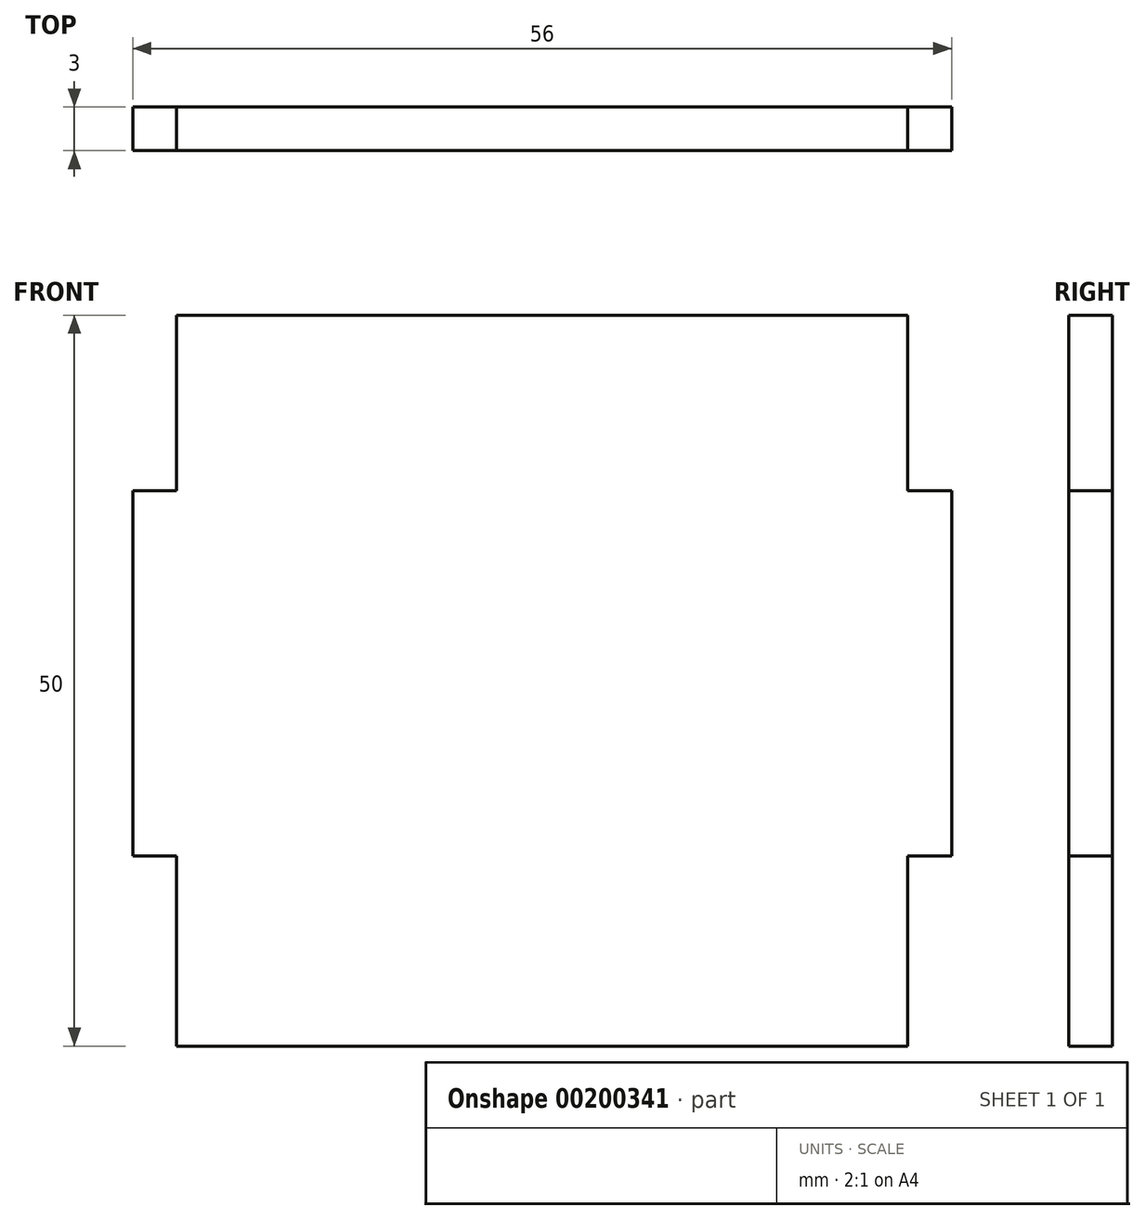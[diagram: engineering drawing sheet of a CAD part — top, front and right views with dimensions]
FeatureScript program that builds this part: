
annotation { "Feature Type Name" : "Feature", "Feature Type Description" : "" }
export const myFeature = defineFeature(function(context is Context, id is Id, definition is map)
    precondition{}
    {
        {
            var Q0;
            Q0=qCreatedBy(makeId("Front.planeOp"),FACE);
            var sketch = newSketch(context, id + "F0", { "sketchPlane" : qUnion([Q0])});
            skLineSegment(sketch, "E0.bottom", {"start": v(-60.5, 25.67) * mm, "end": v(-10.5, 25.67) * mm});
            skLineSegment(sketch, "E0.top", {"start": v(-60.5, -24.33) * mm, "end": v(-10.5, -24.33) * mm});
            skLineSegment(sketch, "E0.left", {"start": v(-60.5, 25.67) * mm, "end": v(-60.5, -24.33) * mm});
            skLineSegment(sketch, "E0.right", {"start": v(-10.5, 25.67) * mm, "end": v(-10.5, -24.33) * mm});
            skSolve(sketch);
        }
        {
            var Q0;
            Q0 = qSketchRegion(id + "F0", true);
            extrude(context, id + "F1", {"entities" : qUnion([Q0]), "depth" : 3 * mm});
        }
        {
            var Q0;
            Q0=makeQuery(id+"F1.opExtrude","SWEPT_FACE",FACE,{"disambiguationData":[OSD([sQuery(id+"F0.wireOp",EDGE,"E0.right")])]});
            var sketch = newSketch(context, id + "F2", { "sketchPlane" : qUnion([Q0])});
            skLineSegment(sketch, "E1.bottom", {"start": v(-3, 13.67) * mm, "end": v(0, 13.67) * mm});
            skLineSegment(sketch, "E1.top", {"start": v(-3, -11.33) * mm, "end": v(0, -11.33) * mm});
            skLineSegment(sketch, "E1.left", {"start": v(-3, 13.67) * mm, "end": v(-3, -11.33) * mm});
            skLineSegment(sketch, "E1.right", {"start": v(0, 13.67) * mm, "end": v(0, -11.33) * mm});
            skSolve(sketch);
        }
        {
            var Q0;
            Q0 = qSketchRegion(id + "F2", true);
            extrude(context, id + "F3", {"entities" : qUnion([Q0]), "operationType" : NewBodyOperationType.ADD, "depth" : 3 * mm});
        }
        {
            var Q0;
            Q0=makeQuery(id+"F1.opExtrude","SWEPT_FACE",FACE,{"disambiguationData":[OSD([sQuery(id+"F0.wireOp",EDGE,"E0.left")])]});
            var sketch = newSketch(context, id + "F4", { "sketchPlane" : qUnion([Q0])});
            skLineSegment(sketch, "E2.bottom", {"start": v(0, -11.33) * mm, "end": v(3, -11.33) * mm});
            skLineSegment(sketch, "E2.top", {"start": v(0, 13.67) * mm, "end": v(3, 13.67) * mm});
            skLineSegment(sketch, "E2.left", {"start": v(0, -11.33) * mm, "end": v(0, 13.67) * mm});
            skLineSegment(sketch, "E2.right", {"start": v(3, -11.33) * mm, "end": v(3, 13.67) * mm});
            skSolve(sketch);
        }
        {
            var Q0;
            Q0 = qSketchRegion(id + "F4", true);
            extrude(context, id + "F5", {"entities" : qUnion([Q0]), "operationType" : NewBodyOperationType.ADD, "depth" : 3 * mm});
        }
    });
